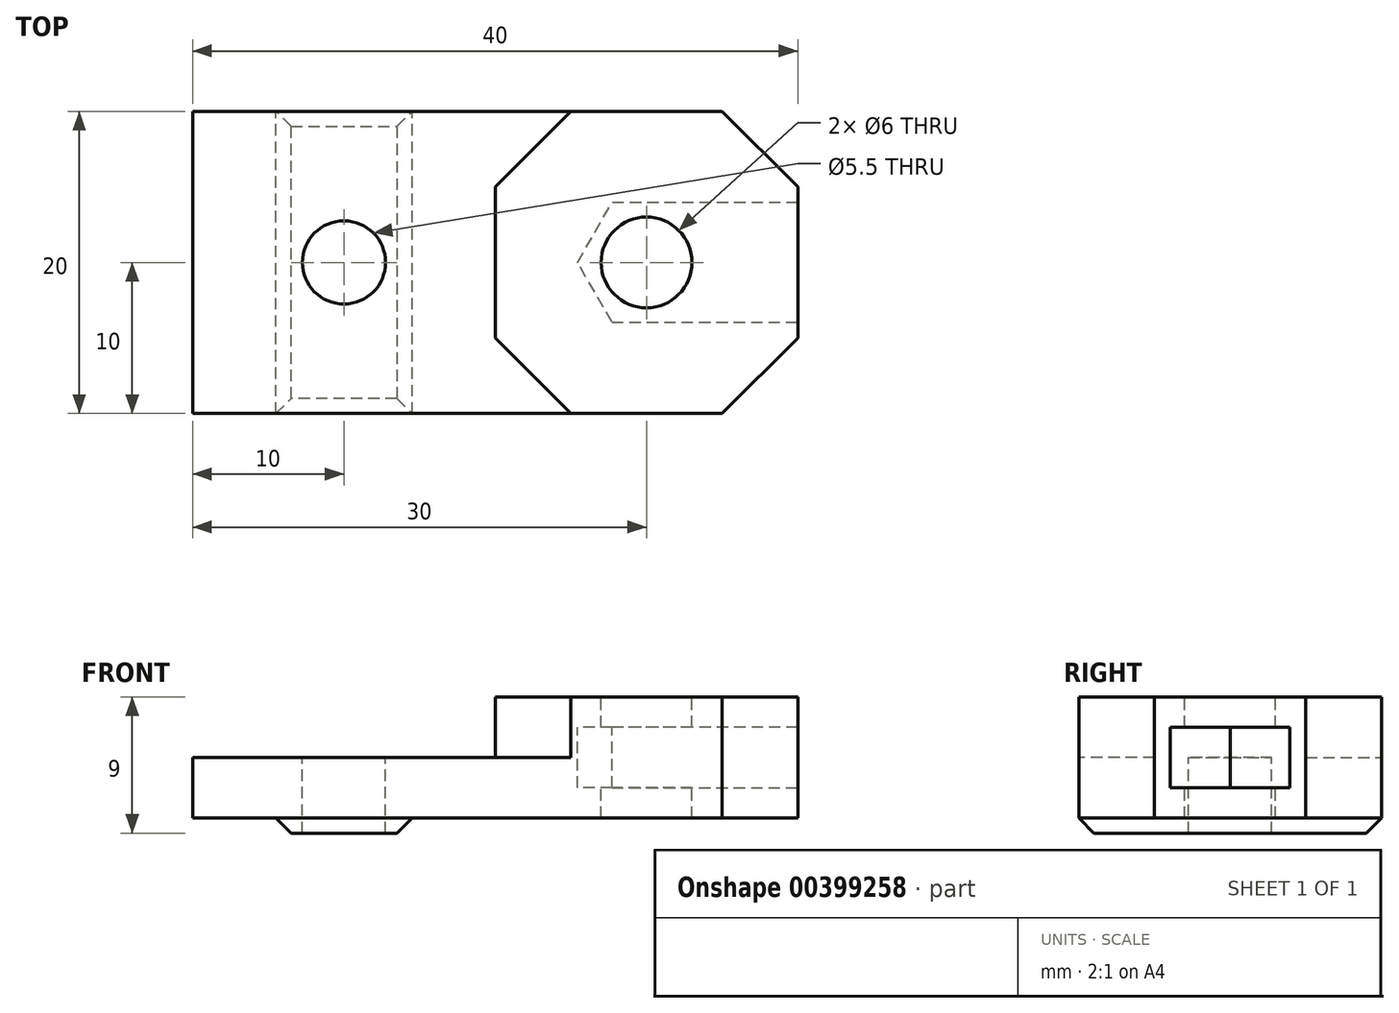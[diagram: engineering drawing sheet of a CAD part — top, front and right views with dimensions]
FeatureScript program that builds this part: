
annotation { "Feature Type Name" : "Feature", "Feature Type Description" : "" }
export const myFeature = defineFeature(function(context is Context, id is Id, definition is map)
    precondition{}
    {
        {
            var Q0;
            Q0=qCreatedBy(makeId("Top.planeOp"),FACE);
            var sketch = newSketch(context, id + "F0", { "sketchPlane" : qUnion([Q0])});
            skLineSegment(sketch, "E0.bottom", {"start": v(0, 0) * mm, "end": v(40, 0) * mm});
            skLineSegment(sketch, "E0.top", {"start": v(0, 20) * mm, "end": v(40, 20) * mm});
            skLineSegment(sketch, "E0.left", {"start": v(0, 0) * mm, "end": v(0, 20) * mm});
            skLineSegment(sketch, "E0.right", {"start": v(40, 0) * mm, "end": v(40, 20) * mm});
            skSolve(sketch);
        }
        {
            var Q0;
            Q0 = qSketchRegion(id + "F0", true);
            extrude(context, id + "F1", {"entities" : qUnion([Q0]), "depth" : 4 * mm});
        }
        {
            var Q0;
            Q0=makeQuery(id+"F1.opExtrude","CAP_FACE",FACE,{"disambiguationData":[OSD([sQuery(id+"F0.wireOp",EDGE,"E0.bottom"),sQuery(id+"F0.wireOp",EDGE,"E0.top"),sQuery(id+"F0.wireOp",EDGE,"E0.left"),sQuery(id+"F0.wireOp",EDGE,"E0.right")])],"isStart":false});
            var sketch = newSketch(context, id + "F2", { "sketchPlane" : qUnion([Q0])});
            skLineSegment(sketch, "E1.bottom", {"start": v(40, 20) * mm, "end": v(20, 20) * mm});
            skLineSegment(sketch, "E1.top", {"start": v(40, 0) * mm, "end": v(20, 0) * mm});
            skLineSegment(sketch, "E1.left", {"start": v(40, 20) * mm, "end": v(40, 0) * mm});
            skLineSegment(sketch, "E1.right", {"start": v(20, 20) * mm, "end": v(20, 0) * mm});
            skSolve(sketch);
        }
        {
            var Q0;
            Q0=makeQuery(id+"F2.imprint","IMPRINT",FACE,{"disambiguationData":[TD([[makeQuery(id+"F2.imprint","IMPRINT",EDGE,{"derivedFrom":sQuery(id+"F2.wireOp",EDGE,"E1.bottom")}),-1.0]])]});
            extrude(context, id + "F3", {"entities" : qUnion([Q0]), "operationType" : NewBodyOperationType.ADD, "depth" : 4 * mm});
        }
        {
            var Q0;
            Q0=makeQuery(id+"F1.opExtrude","CAP_FACE",FACE,{"disambiguationData":[OSD([sQuery(id+"F0.wireOp",EDGE,"E0.bottom"),sQuery(id+"F0.wireOp",EDGE,"E0.top"),sQuery(id+"F0.wireOp",EDGE,"E0.left"),sQuery(id+"F0.wireOp",EDGE,"E0.right")])],"isStart":true});
            var sketch = newSketch(context, id + "F4", { "sketchPlane" : qUnion([Q0])});
            skLineSegment(sketch, "E2.bottom", {"start": v(5.5, 0) * mm, "end": v(14.5, 0) * mm});
            skLineSegment(sketch, "E2.top", {"start": v(5.5, -20) * mm, "end": v(14.5, -20) * mm});
            skLineSegment(sketch, "E2.left", {"start": v(5.5, 0) * mm, "end": v(5.5, -20) * mm});
            skLineSegment(sketch, "E2.right", {"start": v(14.5, 0) * mm, "end": v(14.5, -20) * mm});
            skSolve(sketch);
        }
        {
            var Q0;
            Q0=makeQuery(id+"F4.imprint","IMPRINT",FACE,{"disambiguationData":[TD([[makeQuery(id+"F4.imprint","IMPRINT",EDGE,{"derivedFrom":sQuery(id+"F4.wireOp",EDGE,"E2.bottom")}),-1.0]])]});
            extrude(context, id + "F5", {"entities" : qUnion([Q0]), "operationType" : NewBodyOperationType.ADD, "depth" : 1 * mm});
        }
        {
            var Q0;
            Q0=makeQuery(id+"F5.opExtrude","CAP_FACE",FACE,{"disambiguationData":[OSD([sQuery(id+"F4.wireOp",EDGE,"E2.bottom"),sQuery(id+"F4.wireOp",EDGE,"E2.top"),sQuery(id+"F4.wireOp",EDGE,"E2.left"),sQuery(id+"F4.wireOp",EDGE,"E2.right")])],"isStart":false});
            chamfer(context, id + "F6", {"entities" : qUnion([Q0]), "width" : 1 * mm, "tangentPropagation" : true});
        }
        {
            var Q0;
            Q0=makeQuery(id+"F1.opExtrude","CAP_FACE",FACE,{"disambiguationData":[OSD([sQuery(id+"F0.wireOp",EDGE,"E0.bottom"),sQuery(id+"F0.wireOp",EDGE,"E0.top"),sQuery(id+"F0.wireOp",EDGE,"E0.left"),sQuery(id+"F0.wireOp",EDGE,"E0.right")])],"isStart":false});
            var sketch = newSketch(context, id + "F7", { "sketchPlane" : qUnion([Q0])});
            skCircle(sketch, "E3", {"center": v(10, 10) * mm, "radius": 2.75 * mm});
            skPoint(sketch, "E3.centerSnap0", {"position": v(0, 10) * mm});
            skPoint(sketch, "E3.centerSnap1", {"position": v(10, 20) * mm});
            skSolve(sketch);
        }
        {
            var Q0;
            Q0=makeQuery(id+"F7.imprint","IMPRINT",FACE,{"disambiguationData":[TD([[makeQuery(id+"F7.imprint","IMPRINT",EDGE,{"derivedFrom":sQuery(id+"F7.wireOp",EDGE,"E3")}),1.0]])]});
            extrude(context, id + "F8", {"entities" : qUnion([Q0]), "operationType" : NewBodyOperationType.REMOVE, "endBound" : BoundingType.THROUGH_ALL, "oppositeDirection" : true, "depth" : 25 * mm});
        }
        {
            var Q0;
            Q0=makeQuery(id+"F3.boolean.opBoolean","MERGE",EDGE,{"derivedFrom":[makeQuery(id+"F1.opExtrude","SWEPT_EDGE",EDGE,{"disambiguationData":[OSD([sQuery(id+"F0.wireOp",EDGE,"E0.bottom"),sQuery(id+"F0.wireOp",EDGE,"E0.right")])]}),makeQuery(id+"F3.opExtrude","SWEPT_EDGE",EDGE,{"disambiguationData":[OSD([sQuery(id+"F2.wireOp",EDGE,"E1.top"),sQuery(id+"F2.wireOp",EDGE,"E1.left")])]})]});
            var Q1;
            Q1=makeQuery(id+"F3.boolean.opBoolean","MERGE",EDGE,{"derivedFrom":[makeQuery(id+"F1.opExtrude","SWEPT_EDGE",EDGE,{"disambiguationData":[OSD([sQuery(id+"F0.wireOp",EDGE,"E0.top"),sQuery(id+"F0.wireOp",EDGE,"E0.right")])]}),makeQuery(id+"F3.opExtrude","SWEPT_EDGE",EDGE,{"disambiguationData":[OSD([sQuery(id+"F2.wireOp",EDGE,"E1.bottom"),sQuery(id+"F2.wireOp",EDGE,"E1.left")])]})]});
            var Q2;
            Q2=makeQuery(id+"F3.opExtrude","SWEPT_EDGE",EDGE,{"disambiguationData":[OSD([sQuery(id+"F0.wireOp",EDGE,"E0.bottom"),sQuery(id+"F2.wireOp",EDGE,"E1.top"),sQuery(id+"F2.wireOp",EDGE,"E1.right")])]});
            var Q3;
            Q3=makeQuery(id+"F3.opExtrude","SWEPT_EDGE",EDGE,{"disambiguationData":[OSD([sQuery(id+"F0.wireOp",EDGE,"E0.top"),sQuery(id+"F2.wireOp",EDGE,"E1.bottom"),sQuery(id+"F2.wireOp",EDGE,"E1.right")])]});
            chamfer(context, id + "F9", {"entities" : qUnion([Q0, Q1, Q2, Q3]), "width" : 5 * mm, "tangentPropagation" : true});
        }
        {
            var Q0;
            Q0=makeQuery(id+"F3.opExtrude","CAP_FACE",FACE,{"disambiguationData":[OSD([sQuery(id+"F2.wireOp",EDGE,"E1.bottom"),sQuery(id+"F2.wireOp",EDGE,"E1.top"),sQuery(id+"F2.wireOp",EDGE,"E1.left"),sQuery(id+"F2.wireOp",EDGE,"E1.right")])],"isStart":false});
            var sketch = newSketch(context, id + "F10", { "sketchPlane" : qUnion([Q0])});
            skCircle(sketch, "E4", {"center": v(30, 10) * mm, "radius": 3 * mm});
            skPoint(sketch, "E4.centerSnap0", {"position": v(30, 20) * mm});
            skPoint(sketch, "E4.centerSnap1", {"position": v(20, 10) * mm});
            skSolve(sketch);
        }
        {
            var Q0;
            Q0=makeQuery(id+"F10.imprint","IMPRINT",FACE,{"disambiguationData":[TD([[makeQuery(id+"F10.imprint","IMPRINT",EDGE,{"derivedFrom":sQuery(id+"F10.wireOp",EDGE,"E4")}),1.0]])]});
            extrude(context, id + "F11", {"entities" : qUnion([Q0]), "operationType" : NewBodyOperationType.REMOVE, "endBound" : BoundingType.THROUGH_ALL, "oppositeDirection" : true, "depth" : 25 * mm});
        }
        {
            var Q0;
            Q0=makeQuery(id+"F1.opExtrude","CAP_FACE",FACE,{"disambiguationData":[OSD([sQuery(id+"F0.wireOp",EDGE,"E0.bottom"),sQuery(id+"F0.wireOp",EDGE,"E0.top"),sQuery(id+"F0.wireOp",EDGE,"E0.left"),sQuery(id+"F0.wireOp",EDGE,"E0.right")])],"isStart":false});
            var sketch = newSketch(context, id + "F12", { "sketchPlane" : qUnion([Q0])});
            skCircle(sketch, "E5.0", {"center": v(30, 10) * mm, "radius": 3 * mm, "construction": true});
            skCircle(sketch, "E6.cCircle", {"center": v(30, 10) * mm, "radius": 3.95 * mm, "construction": true});
            skLineSegment(sketch, "E6.0", {"start": v(27.72, 13.95) * mm, "end": v(32.28, 13.95) * mm, "construction": true});
            skLineSegment(sketch, "E6.1", {"start": v(32.28, 13.95) * mm, "end": v(34.56, 10) * mm, "construction": true});
            skLineSegment(sketch, "E6.2", {"start": v(34.56, 10) * mm, "end": v(32.28, 6.05) * mm, "construction": true});
            skLineSegment(sketch, "E6.3", {"start": v(32.28, 6.05) * mm, "end": v(27.72, 6.05) * mm, "construction": true});
            skLineSegment(sketch, "E6.4", {"start": v(27.72, 6.05) * mm, "end": v(25.44, 10) * mm});
            skLineSegment(sketch, "E6.5", {"start": v(25.44, 10) * mm, "end": v(27.72, 13.95) * mm});
            skPoint(sketch, "E6.0.midPoint", {"position": v(30, 13.95) * mm});
            skLineSegment(sketch, "E7.0.0", {"start": v(35, 20) * mm, "end": v(25, 20) * mm, "construction": true});
            skLineSegment(sketch, "E7.0.1", {"start": v(25, 20) * mm, "end": v(20, 15) * mm, "construction": true});
            skLineSegment(sketch, "E7.0.2", {"start": v(20, 15) * mm, "end": v(20, 5) * mm, "construction": true});
            skLineSegment(sketch, "E7.0.3", {"start": v(20, 5) * mm, "end": v(25, 0) * mm, "construction": true});
            skLineSegment(sketch, "E7.0.4", {"start": v(25, 0) * mm, "end": v(35, 0) * mm, "construction": true});
            skLineSegment(sketch, "E7.0.5", {"start": v(35, 0) * mm, "end": v(40, 5) * mm, "construction": true});
            skLineSegment(sketch, "E7.0.6", {"start": v(40, 5) * mm, "end": v(40, 15) * mm, "construction": true});
            skLineSegment(sketch, "E7.0.7", {"start": v(40, 15) * mm, "end": v(35, 20) * mm, "construction": true});
            skLineSegment(sketch, "E8", {"start": v(27.72, 6.05) * mm, "end": v(40, 6.05) * mm});
            skLineSegment(sketch, "E9", {"start": v(40, 6.05) * mm, "end": v(40, 13.95) * mm});
            skLineSegment(sketch, "E10", {"start": v(40, 13.95) * mm, "end": v(27.72, 13.95) * mm});
            skSolve(sketch);
        }
        {
            var Q0;
            Q0 = qSketchRegion(id + "F12", true);
            extrude(context, id + "F13", {"entities" : qUnion([Q0]), "operationType" : NewBodyOperationType.REMOVE, "endBound" : BoundingType.SYMMETRIC, "oppositeDirection" : true, "depth" : 4 * mm});
        }
    });
